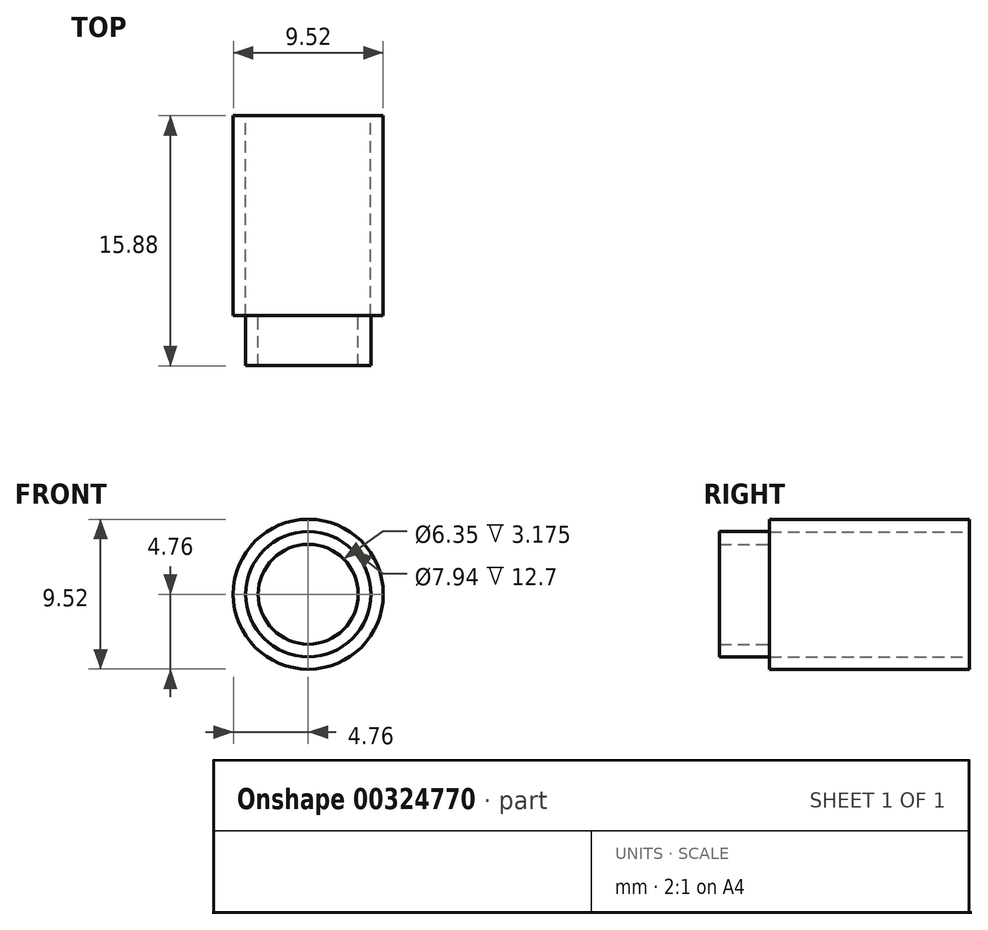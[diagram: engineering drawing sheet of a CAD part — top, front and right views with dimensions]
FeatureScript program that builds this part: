
annotation { "Feature Type Name" : "Feature", "Feature Type Description" : "" }
export const myFeature = defineFeature(function(context is Context, id is Id, definition is map)
    precondition{}
    {
        {
            var Q0;
            Q0=qCreatedBy(makeId("Front.planeOp"),FACE);
            var sketch = newSketch(context, id + "F0", { "sketchPlane" : qUnion([Q0])});
            skCircle(sketch, "E0", {"center": v(0, 0) * mm, "radius": 4.76 * mm});
            skCircle(sketch, "E1", {"center": v(0, 0) * mm, "radius": 3.18 * mm});
            skSolve(sketch);
        }
        {
            var Q0;
            Q0=makeQuery(id+"F0.imprint","IMPRINT",FACE,{"disambiguationData":[TD([[makeQuery(id+"F0.imprint","IMPRINT",EDGE,{"derivedFrom":sQuery(id+"F0.wireOp",EDGE,"E0")}),1.0]])]});
            extrude(context, id + "F1", {"entities" : qUnion([Q0]), "depth" : 15.88 * mm, "offsetDistance" : 25.4 * mm});
        }
        {
            var Q0;
            Q0=makeQuery(id+"F1.opExtrude","CAP_FACE",FACE,{"disambiguationData":[OSD([sQuery(id+"F0.wireOp",EDGE,"E0"),sQuery(id+"F0.wireOp",EDGE,"E1")])],"isStart":false});
            var sketch = newSketch(context, id + "F2", { "sketchPlane" : qUnion([Q0])});
            skCircle(sketch, "E2", {"center": v(0, 0) * mm, "radius": 3.98 * mm});
            skSolve(sketch);
        }
        {
            var Q0;
            Q0=makeQuery(id+"F2.imprint","IMPRINT",FACE,{"disambiguationData":[TD([[makeQuery(id+"F2.imprint","IMPRINT",EDGE,{"derivedFrom":sQuery(id+"F2.wireOp",EDGE,"E2")}),-1.0]])]});
            extrude(context, id + "F3", {"entities" : qUnion([Q0]), "operationType" : NewBodyOperationType.REMOVE, "oppositeDirection" : true, "depth" : 3.17 * mm, "offsetDistance" : 25.4 * mm});
        }
        {
            var Q0;
            Q0=makeQuery(id+"F1.opExtrude","CAP_FACE",FACE,{"disambiguationData":[OSD([sQuery(id+"F0.wireOp",EDGE,"E0"),sQuery(id+"F0.wireOp",EDGE,"E1")])],"isStart":true});
            var sketch = newSketch(context, id + "F4", { "sketchPlane" : qUnion([Q0])});
            skCircle(sketch, "E3", {"center": v(0, 0) * mm, "radius": 3.97 * mm});
            skSolve(sketch);
        }
        {
            var Q0;
            Q0=makeQuery(id+"F4.imprint","IMPRINT",FACE,{"disambiguationData":[TD([[makeQuery(id+"F4.imprint","IMPRINT",EDGE,{"derivedFrom":sQuery(id+"F4.wireOp",EDGE,"E3")}),1.0]])]});
            extrude(context, id + "F5", {"entities" : qUnion([Q0]), "operationType" : NewBodyOperationType.REMOVE, "oppositeDirection" : true, "depth" : 12.7 * mm, "offsetDistance" : 25.4 * mm});
        }
    });
